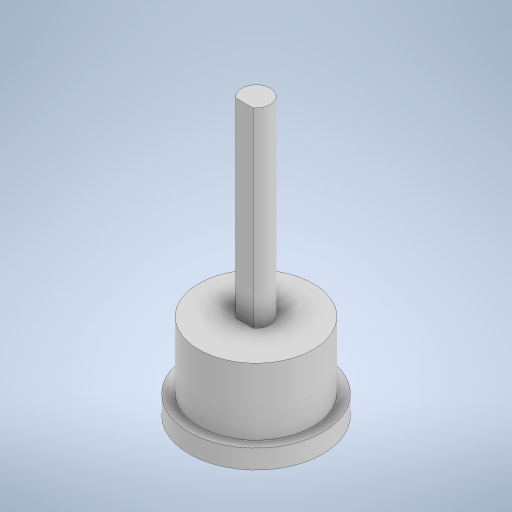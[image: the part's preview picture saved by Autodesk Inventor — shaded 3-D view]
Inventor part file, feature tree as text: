
AUTODESK INVENTOR PART (.ipt)
format: ipt  version: 2023 (Build 270158000, 158)  size: 254,976 bytes
history: native  units: in
note: dims shown in document units (in); Inventor stores cm internally (conversion verified against a paired STEP export)
features: extrude x3, sketch x3
ambient origin geometry x8: Origin, YZ Plane, XZ Plane, XY Plane, X Axis, Y Axis, Z Axis, Center Point
bodies: Solid1 (feature_tree)
feature tree (6):
  extrude  "Extrusion1"  Depth=0.2756in TaperAngle=0.0deg
  extrude  "Extrusion2"  Depth=0.1063in
  extrude  "Extrusion3"  Depth=0.0787in
  sketch  "Sketch1"  dims[d0=0.4724in d1=0.2756in d2=0.0in]
  sketch  "Sketch2"  dims[d3=0.1181in d5=0.1063in]
  sketch  "Sketch3"  dims[d6=0.7874in d7=0.0in d8=0.5512in d9=0.0787in d10=0.0in]
